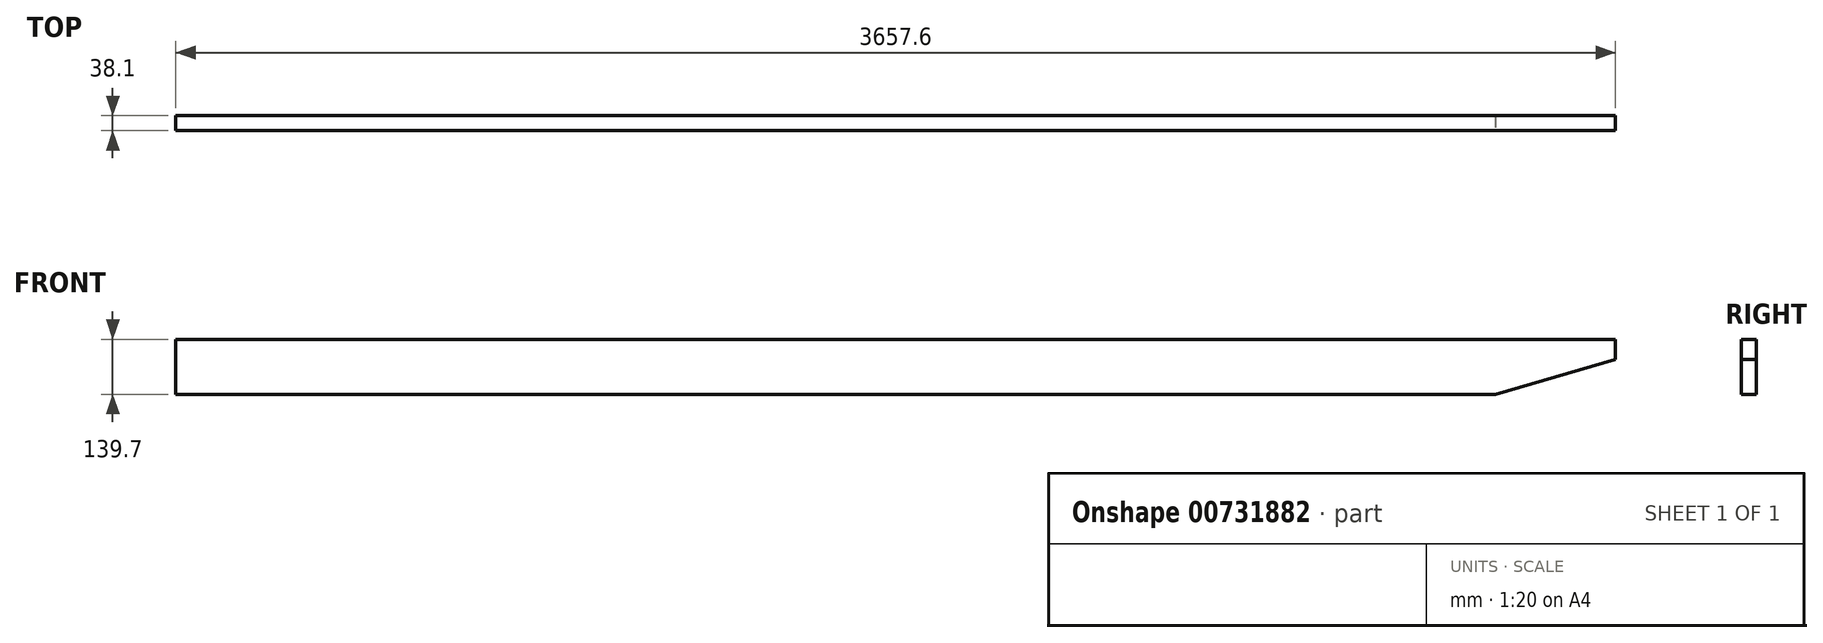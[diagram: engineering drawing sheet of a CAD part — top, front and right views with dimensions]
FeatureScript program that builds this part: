
annotation { "Feature Type Name" : "Feature", "Feature Type Description" : "" }
export const myFeature = defineFeature(function(context is Context, id is Id, definition is map)
    precondition{}
    {
        {
            var Q0;
            Q0=qCreatedBy(makeId("Right.planeOp"),FACE);
            var sketch = newSketch(context, id + "F0", { "sketchPlane" : qUnion([Q0])});
            skLineSegment(sketch, "E0.bottom", {"start": v(0, 0) * mm, "end": v(38.1, 0) * mm});
            skLineSegment(sketch, "E0.top", {"start": v(0, 139.7) * mm, "end": v(38.1, 139.7) * mm});
            skLineSegment(sketch, "E0.left", {"start": v(0, 0) * mm, "end": v(0, 139.7) * mm});
            skLineSegment(sketch, "E0.right", {"start": v(38.1, 0) * mm, "end": v(38.1, 139.7) * mm});
            skSolve(sketch);
        }
        {
            var Q0;
            Q0=makeQuery(id+"F0.imprint","IMPRINT",FACE,{"disambiguationData":[TD([[makeQuery(id+"F0.imprint","IMPRINT",EDGE,{"derivedFrom":sQuery(id+"F0.wireOp",EDGE,"E0.bottom")}),1.0]])]});
            extrude(context, id + "F1", {"entities" : qUnion([Q0]), "depth" : 3657.6 * mm, "offsetDistance" : 25.4 * mm});
        }
        {
            var Q0;
            Q0=makeQuery(id+"F1.opExtrude","SWEPT_FACE",FACE,{"disambiguationData":[OSD([sQuery(id+"F0.wireOp",EDGE,"E0.left")])]});
            var sketch = newSketch(context, id + "F2", { "sketchPlane" : qUnion([Q0])});
            skLineSegment(sketch, "E1", {"start": v(3657.6, 0) * mm, "end": v(3657.6, 88.9) * mm});
            skLineSegment(sketch, "E2", {"start": v(3657.6, 88.9) * mm, "end": v(3352.8, 0) * mm});
            skLineSegment(sketch, "E3", {"start": v(3352.8, 0) * mm, "end": v(3657.6, 0) * mm});
            skSolve(sketch);
        }
        {
            var Q0;
            Q0=makeQuery(id+"F2.imprint","IMPRINT",FACE,{"disambiguationData":[TD([[makeQuery(id+"F2.imprint","IMPRINT",EDGE,{"derivedFrom":sQuery(id+"F2.wireOp",EDGE,"E1")}),1.0]])]});
            extrude(context, id + "F3", {"entities" : qUnion([Q0]), "operationType" : NewBodyOperationType.REMOVE, "endBound" : BoundingType.THROUGH_ALL, "oppositeDirection" : true, "depth" : 25.4 * mm, "offsetDistance" : 25.4 * mm});
        }
    });
